# Revit family: ElectricalFixture_Hager_IP66FusedConnectionUnit
name_source: partatom
category: Lighting Fixtures
revit_build: Autodesk Revit 2015 (Build: 20160512_1515(x64)
units: mm (PartAtom-declared; Revit-internal decimal feet)

## types (1)
- WXPSSU83FO
    1Gang = No
    2 Gang = No
    AssetType = Fixed
    BIMObjectName = Hager_ElectricalFixture_WXPSSU83FO
    Back Plate Depth = 39 mm
    Back Plate Height = 90 mm
    Back Plate Width = 90 mm
    Category = ElectricalFixture
    ClassificationName = Uniclass2015
    ClassificationValue = Pr_65_72_97
    Colour = RAL9010WhiteGloss
    Default Elevation = 500 mm
    Description = IP6613ADoublePoleSwitchedFusedConnectionUnitWithFlexOutlet
    DocumentationCertificates = http://www.hager.co.uk
    DocumentationLiterature = http://www.hager.co.uk
    DocumentationTechnical = http://www.hager.co.uk
    DurationUnit = Years
    EAN = 3250617260114
    ExpectedLife = 25
    Extrusion From Wall = 17 mm
    Features = IP6613ADoublePoleSwitchedFusedConnectionUnitWithFlexOutlet
    Frequency = 50/60Hz
    IfcExportAs = ElectricalFixture
    IfcExportType = ElectricalFixture
    Keynote = 16400
    LED Indicator Switch = No
    Manufacturer = Hager
    ManufacturerName = Hager
    Material = Urea Formaldehyde Thermoset Plastic
    Model = WXPSSU83FO
    ModelNumber = WXPSSU83FO
    ModelReference = WXPSSU83FO
    NBSDescription = ElectricalFixture
    NBSObjectName = Hager_IP66FusedConnectionUnit_WXPSSU83FO
    NBSReference = Pr_65_72_97
    NominalDepth = 55 mm
    NominalHeight = 115 mm
    NominalLength = 103 mm
    NominalWidth = 64 mm
    One Way = No
    ReplacementCost = 0
    ServiceLifeDuration = 0
    Shape = Rectangular
    Supply Phase = 1
    Switch = Yes
    Switch Height = 0 mm  [stored 0 ft]
    Switch Width = 0 mm  [stored 0 ft]
    Two Way = Yes
    Type Comments = WXPSSU83FO
    TypeName = ElectricalFixture_IP66FusedConnectionUnit_WXPSSU83FO
    URL = http://www.hager.co.uk
    Voltage = 230V/240V
    WarrantyDescription = See Manufacturer
    WarrantyDurationLabor = 0
    WarrantyDurationParts = 10
    WarrantyDurationUnit = Years
    WarrantyGuarantorParts = 10
    _BimSpecGuid = 0
    _BimstoreBibleVersion = V14
    _CurrentRevision = 0
    _DistributedBy = www.bimstore.co.uk

note: [stored X ft] marks values corroborated as IEEE doubles in the binary element streams (Revit-internal decimal feet)

## geometry (parser evidence)
native form markers: Blend x8, Sweep x2
no freeform markers — native parametric forms only
